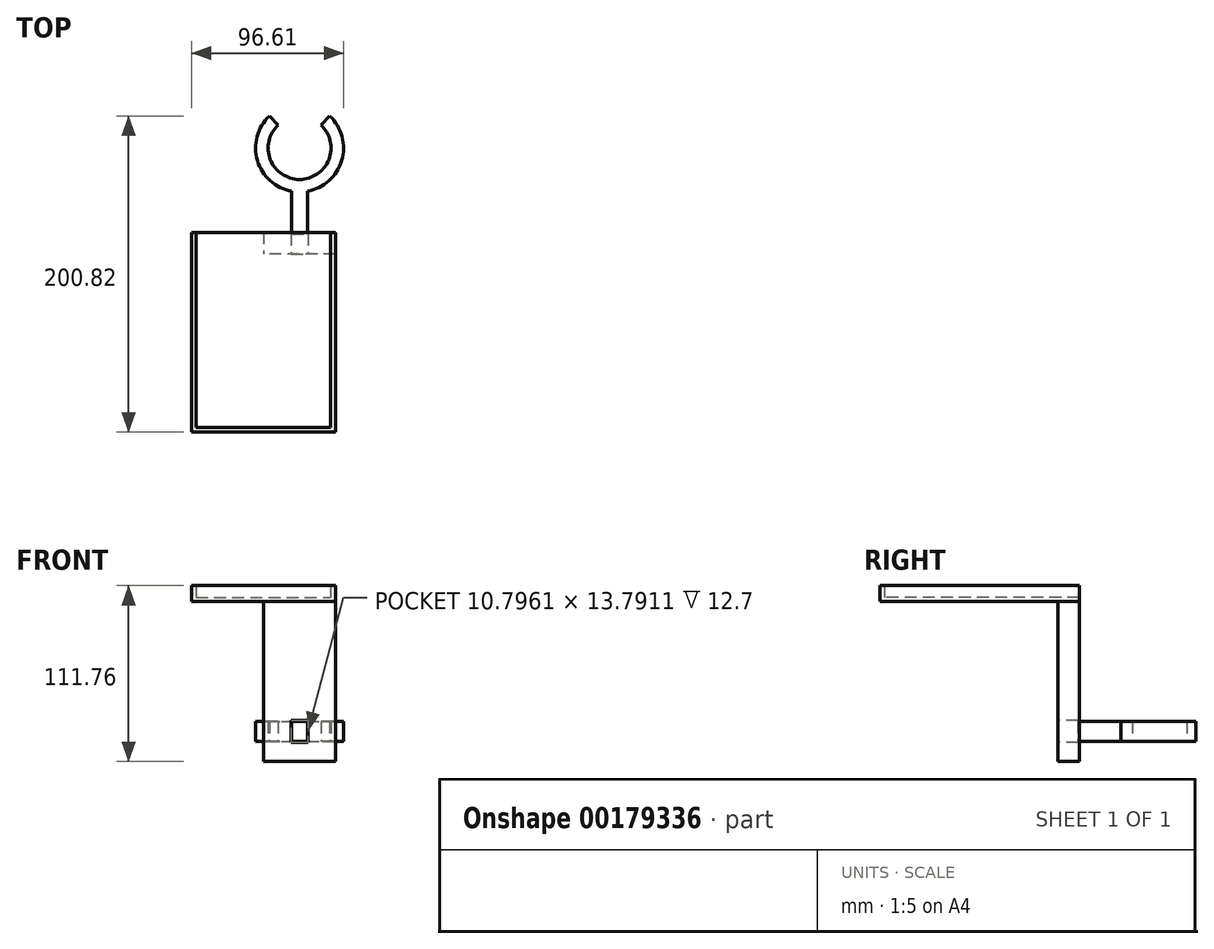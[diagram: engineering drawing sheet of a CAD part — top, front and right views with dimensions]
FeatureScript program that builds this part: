
annotation { "Feature Type Name" : "Feature", "Feature Type Description" : "" }
export const myFeature = defineFeature(function(context is Context, id is Id, definition is map)
    precondition{}
    {
        {
            var Q0;
            Q0=qCreatedBy(makeId("Top.planeOp"),FACE);
            var sketch = newSketch(context, id + "F0", { "sketchPlane" : qUnion([Q0])});
            skLineSegment(sketch, "E0", {"start": v(-4.98, 0) * mm, "end": v(-4.98, -39.77) * mm});
            skArc(sketch, "E1", {"start": v(-4.98, 0) * mm, "mid": v(-26.8, 19.57) * mm, "end": v(-19.15, 47.86) * mm});
            skLineSegment(sketch, "E2", {"start": v(-19.15, 47.86) * mm, "end": v(-13.63, 42.12) * mm});
            skArc(sketch, "E3", {"start": v(-13.63, 42.12) * mm, "mid": v(-18.6, 20.17) * mm, "end": v(0, 7.51) * mm});
            skArc(sketch, "E4.MirrorCS", {"start": v(13.63, 42.12) * mm, "mid": v(18.6, 20.17) * mm, "end": v(0, 7.51) * mm});
            skLineSegment(sketch, "E5.MirrorCS", {"start": v(19.15, 47.86) * mm, "end": v(13.63, 42.12) * mm});
            skLineSegment(sketch, "E6.MirrorCS", {"start": v(4.98, 0) * mm, "end": v(4.98, -39.77) * mm});
            skArc(sketch, "E7.MirrorCS", {"start": v(4.98, 0) * mm, "mid": v(26.8, 19.57) * mm, "end": v(19.15, 47.86) * mm});
            skLineSegment(sketch, "E8", {"start": v(-4.98, -39.77) * mm, "end": v(4.98, -39.77) * mm});
            skSolve(sketch);
        }
        {
            var Q0;
            Q0=makeQuery(id+"F0.imprint","IMPRINT",FACE,{"disambiguationData":[TD([[makeQuery(id+"F0.imprint","IMPRINT",EDGE,{"derivedFrom":sQuery(id+"F0.wireOp",EDGE,"E0")}),1.0]])]});
            extrude(context, id + "F1", {"entities" : qUnion([Q0]), "depth" : 12.7 * mm});
        }
        {
            var Q0;
            Q0=makeQuery(id+"F1.opExtrude","CAP_FACE",FACE,{"disambiguationData":[OSD([sQuery(id+"F0.wireOp",EDGE,"E0"),sQuery(id+"F0.wireOp",EDGE,"fpNfXiwE-KSUs-EZ8J-zToy-EjGe3sr1woA0"),sQuery(id+"F0.wireOp",EDGE,"E1"),sQuery(id+"F0.wireOp",EDGE,"E2"),sQuery(id+"F0.wireOp",EDGE,"E3"),sQuery(id+"F0.wireOp",EDGE,"E4.MirrorCS"),sQuery(id+"F0.wireOp",EDGE,"E5.MirrorCS"),sQuery(id+"F0.wireOp",EDGE,"46a1613c-b0cb-44c9-9270-1d0dd435f8ee2.MirrorCS"),sQuery(id+"F0.wireOp",EDGE,"E6.MirrorCS"),sQuery(id+"F0.wireOp",EDGE,"E7.MirrorCS")])],"isStart":false});
            var sketch = newSketch(context, id + "F2", { "sketchPlane" : qUnion([Q0])});
            skLineSegment(sketch, "E9.left", {"start": v(-22.85, -26.15) * mm, "end": v(-22.85, -39.77) * mm});
            skLineSegment(sketch, "E10.MirrorCS", {"start": v(22.85, -26.15) * mm, "end": v(22.85, -39.77) * mm});
            skLineSegment(sketch, "E11", {"start": v(-22.85, -26.15) * mm, "end": v(22.85, -26.15) * mm});
            skLineSegment(sketch, "E12", {"start": v(22.85, -39.77) * mm, "end": v(-22.85, -39.77) * mm});
            skSolve(sketch);
        }
        {
            var Q0;
            {var subQ0=sQuery(id+"F2.wireOp",EDGE,"E9.left");Q0=makeQuery(id+"F2.imprint","IMPRINT",FACE,{"disambiguationData":[TD([[makeQuery(id+"F2.imprint","IMPRINT",EDGE,{"derivedFrom":subQ0}),1.0]])]});}
            var Q1;
            {var subQ0=sQuery(id+"F2.wireOp",EDGE,"E11");var subQ1=makeQuery(id+"F1.opExtrude","CAP_EDGE",EDGE,{"disambiguationData":[OSD([sQuery(id+"F0.wireOp",EDGE,"E0")])],"isStart":false});var subQ2=makeQuery(id+"F2.imprint","INTERSECT",VERTEX,{"derivedFrom":[subQ1,subQ0]});Q1=makeQuery(id+"F2.imprint","IMPRINT",FACE,{"disambiguationData":[TD([[makeQuery(id+"F2.imprint","IMPRINT",EDGE,{"disambiguationData":[TD([[subQ2,-1.0]])],"derivedFrom":subQ0}),-1.0]])]});}
            var Q2;
            {var subQ0=sQuery(id+"F2.wireOp",EDGE,"E10.MirrorCS");Q2=makeQuery(id+"F2.imprint","IMPRINT",FACE,{"disambiguationData":[TD([[makeQuery(id+"F2.imprint","IMPRINT",EDGE,{"derivedFrom":subQ0}),-1.0]])]});}
            extrude(context, id + "F3", {"entities" : qUnion([Q0, Q1, Q2]), "depth" : 76.2 * mm, "hasSecondDirection" : true, "secondDirectionOppositeDirection" : true, "secondDirectionDepth" : 25.4 * mm});
        }
        {
            var Q0;
            Q0=makeQuery(id+"F3.opExtrude","SWEPT_FACE",FACE,{"disambiguationData":[OSD([sQuery(id+"F2.wireOp",EDGE,"E12")])]});
            var sketch = newSketch(context, id + "F4", { "sketchPlane" : qUnion([Q0])});
            skLineSegment(sketch, "E13.bottom", {"start": v(-5.4, 13.3) * mm, "end": v(5.4, 13.3) * mm});
            skLineSegment(sketch, "E13.top", {"start": v(-5.4, -0.5) * mm, "end": v(5.4, -0.5) * mm});
            skLineSegment(sketch, "E13.left", {"start": v(-5.4, 13.3) * mm, "end": v(-5.4, -0.5) * mm});
            skLineSegment(sketch, "E13.right", {"start": v(5.4, 13.3) * mm, "end": v(5.4, -0.5) * mm});
            skSolve(sketch);
        }
        {
            var Q0;
            Q0=makeQuery(id+"F4.imprint","IMPRINT",FACE,{"disambiguationData":[TD([[makeQuery(id+"F4.imprint","IMPRINT",EDGE,{"derivedFrom":sQuery(id+"F4.wireOp",EDGE,"E13.bottom")}),-1.0]])]});
            extrude(context, id + "F5", {"entities" : qUnion([Q0]), "operationType" : NewBodyOperationType.REMOVE, "oppositeDirection" : true, "depth" : 12.7 * mm});
        }
        {
            var Q0;
            Q0=makeQuery(id+"F3.opExtrude","CAP_FACE",FACE,{"disambiguationData":[OSD([sQuery(id+"F2.wireOp",EDGE,"E9.left"),sQuery(id+"F2.wireOp",EDGE,"E10.MirrorCS"),sQuery(id+"F2.wireOp",EDGE,"E11"),sQuery(id+"F2.wireOp",EDGE,"E12")])],"isStart":false});
            var sketch = newSketch(context, id + "F6", { "sketchPlane" : qUnion([Q0])});
            skLineSegment(sketch, "E14.bottom", {"start": v(22.85, -26.15) * mm, "end": v(-68.66, -26.15) * mm});
            skLineSegment(sketch, "E14.top", {"start": v(22.85, -152.96) * mm, "end": v(-68.66, -152.96) * mm});
            skLineSegment(sketch, "E14.left", {"start": v(22.85, -26.15) * mm, "end": v(22.85, -152.96) * mm});
            skLineSegment(sketch, "E14.right", {"start": v(-68.66, -26.15) * mm, "end": v(-68.66, -152.96) * mm});
            skSolve(sketch);
        }
        {
            var Q0;
            Q0 = qSketchRegion(id + "F6", true);
            extrude(context, id + "F7", {"entities" : qUnion([Q0]), "depth" : 2.54 * mm});
        }
        {
            var Q0;
            Q0=makeQuery(id+"F7.opExtrude","CAP_FACE",FACE,{"disambiguationData":[OSD([sQuery(id+"F6.wireOp",EDGE,"E14.bottom"),sQuery(id+"F6.wireOp",EDGE,"E14.top"),sQuery(id+"F6.wireOp",EDGE,"E14.left"),sQuery(id+"F6.wireOp",EDGE,"E14.right")])],"isStart":false});
            var sketch = newSketch(context, id + "F8", { "sketchPlane" : qUnion([Q0])});
            skLineSegment(sketch, "E15.bottom", {"start": v(-68.66, -26.15) * mm, "end": v(-65.69, -26.15) * mm});
            skLineSegment(sketch, "E15.top", {"start": v(-68.66, -152.96) * mm, "end": v(-65.69, -152.96) * mm});
            skLineSegment(sketch, "E15.left", {"start": v(-68.66, -26.15) * mm, "end": v(-68.66, -152.96) * mm});
            skLineSegment(sketch, "E15.right", {"start": v(-65.69, -26.15) * mm, "end": v(-65.69, -152.96) * mm});
            skLineSegment(sketch, "E16.bottom", {"start": v(22.85, -26.15) * mm, "end": v(19.85, -26.15) * mm});
            skLineSegment(sketch, "E16.top", {"start": v(22.85, -152.96) * mm, "end": v(19.85, -152.96) * mm});
            skLineSegment(sketch, "E16.left", {"start": v(22.85, -26.15) * mm, "end": v(22.85, -152.96) * mm});
            skLineSegment(sketch, "E16.right", {"start": v(19.85, -26.15) * mm, "end": v(19.85, -152.96) * mm});
            skLineSegment(sketch, "E17.bottom", {"start": v(-65.69, -152.96) * mm, "end": v(19.85, -152.96) * mm});
            skLineSegment(sketch, "E17.top", {"start": v(-65.69, -149.89) * mm, "end": v(19.85, -149.89) * mm});
            skLineSegment(sketch, "E17.left", {"start": v(-65.69, -152.96) * mm, "end": v(-65.69, -149.89) * mm});
            skLineSegment(sketch, "E17.right", {"start": v(19.85, -152.96) * mm, "end": v(19.85, -149.89) * mm});
            skSolve(sketch);
        }
        {
            var Q0;
            Q0 = qSketchRegion(id + "F8", true);
            extrude(context, id + "F9", {"entities" : qUnion([Q0]), "operationType" : NewBodyOperationType.ADD, "depth" : 7.62 * mm});
        }
    });
